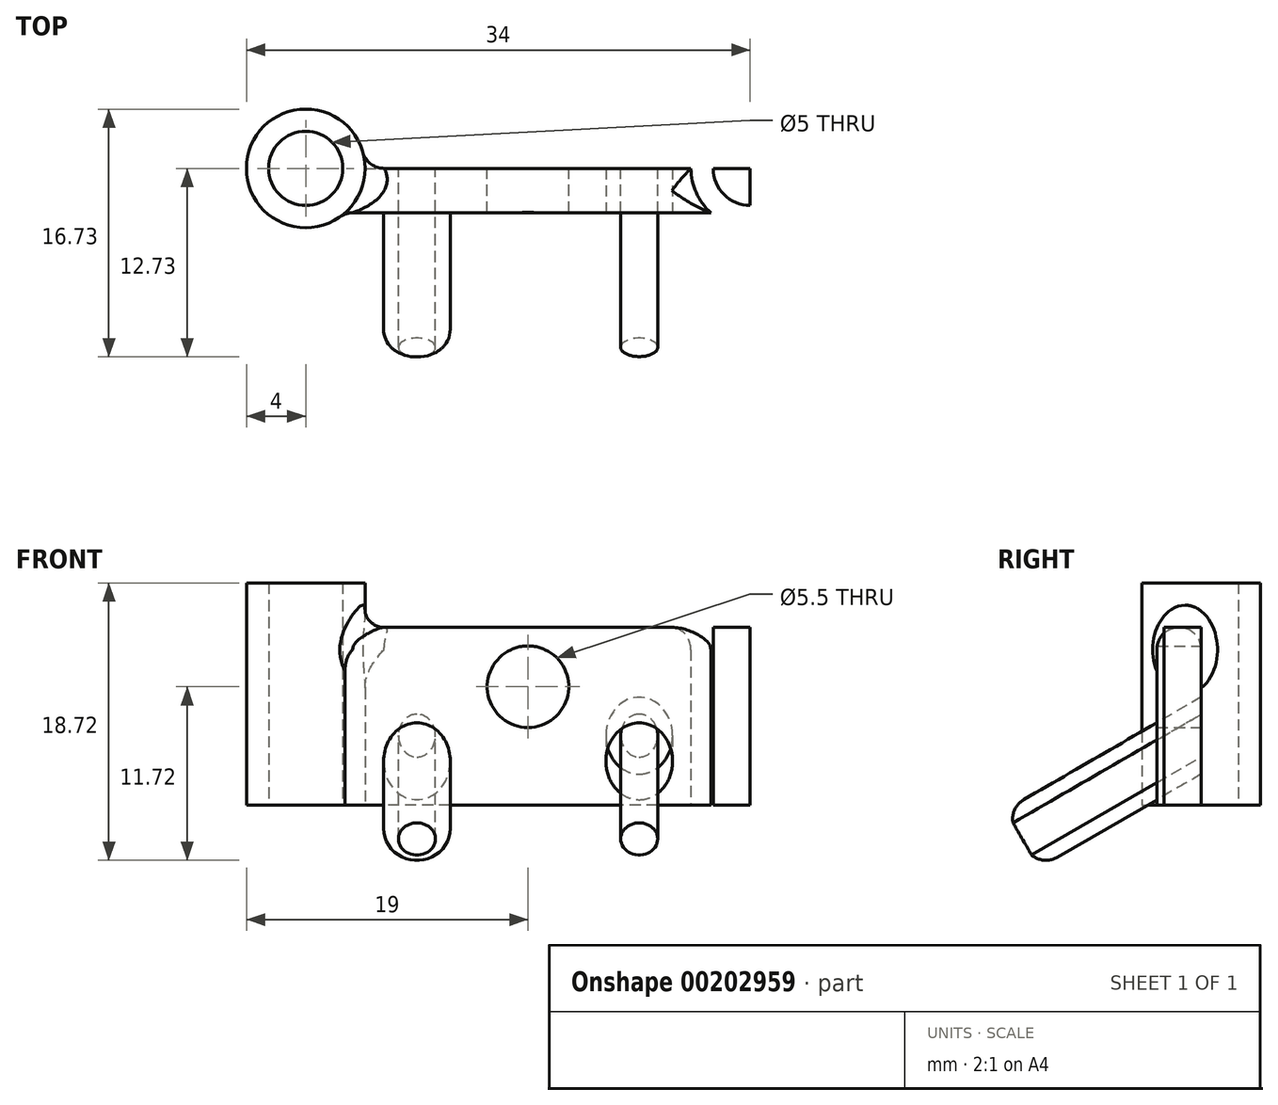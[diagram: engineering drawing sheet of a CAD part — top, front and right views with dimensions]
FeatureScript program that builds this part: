
annotation { "Feature Type Name" : "Feature", "Feature Type Description" : "" }
export const myFeature = defineFeature(function(context is Context, id is Id, definition is map)
    precondition{}
    {
        {
            var Q0;
            Q0=qCreatedBy(makeId("Top.planeOp"),FACE);
            var sketch = newSketch(context, id + "F0", { "sketchPlane" : qUnion([Q0])});
            skCircle(sketch, "E0", {"center": v(-15, 0) * mm, "radius": 2.5 * mm});
            skCircle(sketch, "E1", {"center": v(-15, 0) * mm, "radius": 4 * mm});
            skCircle(sketch, "E2.MirrorC", {"center": v(15, 0) * mm, "radius": 2.5 * mm});
            skCircle(sketch, "E3.MirrorC", {"center": v(15, 0) * mm, "radius": 4 * mm});
            skSolve(sketch);
        }
        {
            var Q0;
            Q0 = qSketchRegion(id + "F0", true);
            extrude(context, id + "F1", {"entities" : qUnion([Q0]), "depth" : 15 * mm, "offsetDistance" : 25 * mm});
        }
        {
            var Q0;
            Q0=qCreatedBy(makeId("Front.planeOp"),FACE);
            var sketch = newSketch(context, id + "F2", { "sketchPlane" : qUnion([Q0])});
            skLineSegment(sketch, "E4.bottom", {"start": v(15, 12) * mm, "end": v(-15, 12) * mm});
            skLineSegment(sketch, "E4.top", {"start": v(15, 0) * mm, "end": v(-15, 0) * mm});
            skLineSegment(sketch, "E4.left", {"start": v(15, 12) * mm, "end": v(15, 0) * mm});
            skLineSegment(sketch, "E4.right", {"start": v(-15, 12) * mm, "end": v(-15, 0) * mm});
            skPoint(sketch, "E4.middle", {"position": v(0, 6) * mm});
            skCircle(sketch, "E5", {"center": v(7.5, 6) * mm, "radius": 1.25 * mm});
            skCircle(sketch, "E6", {"center": v(7.5, 6) * mm, "radius": 2.25 * mm});
            skCircle(sketch, "E7.MirrorC", {"center": v(-7.5, 6) * mm, "radius": 1.25 * mm});
            skCircle(sketch, "E8.MirrorC", {"center": v(-7.5, 6) * mm, "radius": 2.25 * mm});
            skCircle(sketch, "E9", {"center": v(0, 8) * mm, "radius": 2.75 * mm});
            skSolve(sketch);
        }
        {
            var Q0;
            Q0=makeQuery(id+"F2.imprint","IMPRINT",FACE,{"disambiguationData":[TD([[makeQuery(id+"F2.imprint","IMPRINT",EDGE,{"derivedFrom":sQuery(id+"F2.wireOp",EDGE,"E4.bottom")}),1.0]])]});
            var Q1;
            Q1=makeQuery(id+"F2.imprint","IMPRINT",FACE,{"disambiguationData":[TD([[makeQuery(id+"F2.imprint","IMPRINT",EDGE,{"derivedFrom":sQuery(id+"F2.wireOp",EDGE,"E5")}),-1.0]])]});
            var Q2;
            Q2=makeQuery(id+"F2.imprint","IMPRINT",FACE,{"disambiguationData":[TD([[makeQuery(id+"F2.imprint","IMPRINT",EDGE,{"derivedFrom":sQuery(id+"F2.wireOp",EDGE,"E5")}),1.0]])]});
            var Q3;
            Q3=makeQuery(id+"F2.imprint","IMPRINT",FACE,{"disambiguationData":[TD([[makeQuery(id+"F2.imprint","IMPRINT",EDGE,{"derivedFrom":sQuery(id+"F2.wireOp",EDGE,"E7.MirrorC")}),1.0]])]});
            var Q4;
            Q4=makeQuery(id+"F2.imprint","IMPRINT",FACE,{"disambiguationData":[TD([[makeQuery(id+"F2.imprint","IMPRINT",EDGE,{"derivedFrom":sQuery(id+"F2.wireOp",EDGE,"E7.MirrorC")}),-1.0]])]});
            extrude(context, id + "F3", {"entities" : qUnion([Q0, Q1, Q2, Q3, Q4]), "depth" : 3 * mm, "offsetDistance" : 25 * mm});
        }
        {
            var Q0;
            Q0=qCreatedBy(makeId("Front.planeOp"),FACE);
            var Q1;
            Q1=makeQuery(id+"F3.opExtrude","CAP_EDGE",EDGE,{"disambiguationData":[OSD([sQuery(id+"F2.wireOp",EDGE,"E4.bottom")])],"isStart":false});
            cPlane(context, id + "F4", {"entities" : qUnion([Q0, Q1]), "cplaneType" : CPlaneType.LINE_ANGLE, "offset" : 25 * mm, "angle" : 30 * degree, "oppositeDirection" : true, "width" : 150 * mm, "height" : 150 * mm});
        }
        {
            var Q0;
            Q0=qCreatedBy(id+"F4.planeOp",FACE);
            var sketch = newSketch(context, id + "F5", { "sketchPlane" : qUnion([Q0])});
            skLineSegment(sketch, "E10.bottom", {"start": v(15, 13.07) * mm, "end": v(-15, 13.07) * mm});
            skLineSegment(sketch, "E10.top", {"start": v(15, 1.07) * mm, "end": v(-15, 1.07) * mm});
            skLineSegment(sketch, "E10.left", {"start": v(15, 13.07) * mm, "end": v(15, 1.07) * mm});
            skLineSegment(sketch, "E10.right", {"start": v(-15, 13.07) * mm, "end": v(-15, 1.07) * mm});
            skCircle(sketch, "E11", {"center": v(7.5, 4.07) * mm, "radius": 1.25 * mm});
            skCircle(sketch, "E12", {"center": v(7.5, 4.07) * mm, "radius": 2.25 * mm});
            skCircle(sketch, "E13.MirrorC", {"center": v(-7.5, 4.07) * mm, "radius": 1.25 * mm});
            skCircle(sketch, "E14.MirrorC", {"center": v(-7.5, 4.07) * mm, "radius": 2.25 * mm});
            skSolve(sketch);
        }
        {
            var Q0;
            Q0=makeQuery(id+"F5.imprint","IMPRINT",FACE,{"disambiguationData":[TD([[makeQuery(id+"F5.imprint","IMPRINT",EDGE,{"derivedFrom":sQuery(id+"F5.wireOp",EDGE,"E11")}),-1.0]])]});
            var Q1;
            Q1=makeQuery(id+"F5.imprint","IMPRINT",FACE,{"disambiguationData":[TD([[makeQuery(id+"F5.imprint","IMPRINT",EDGE,{"derivedFrom":sQuery(id+"F5.wireOp",EDGE,"E13.MirrorC")}),1.0]])]});
            extrude(context, id + "F6", {"entities" : qUnion([Q0, Q1]), "operationType" : NewBodyOperationType.ADD, "oppositeDirection" : true, "depth" : 15 * mm, "offsetDistance" : 25 * mm, "hasSecondDirection" : true, "secondDirectionOppositeDirection" : false, "secondDirectionDepth" : -3 * mm});
        }
        {
            var Q0;
            Q0=makeQuery(id+"F5.imprint","IMPRINT",FACE,{"disambiguationData":[TD([[makeQuery(id+"F5.imprint","IMPRINT",EDGE,{"derivedFrom":sQuery(id+"F5.wireOp",EDGE,"E11")}),1.0]])]});
            var Q1;
            Q1=makeQuery(id+"F5.imprint","IMPRINT",FACE,{"disambiguationData":[TD([[makeQuery(id+"F5.imprint","IMPRINT",EDGE,{"derivedFrom":sQuery(id+"F5.wireOp",EDGE,"E13.MirrorC")}),-1.0]])]});
            extrude(context, id + "F7", {"entities" : qUnion([Q0, Q1]), "operationType" : NewBodyOperationType.REMOVE, "depth" : 25 * mm, "offsetDistance" : 25 * mm, "hasSecondDirection" : true, "secondDirectionOppositeDirection" : true, "secondDirectionDepth" : 25 * mm});
        }
        {
            var Q0;
            Q0=makeQuery(id+"F3.opExtrude","SWEPT_BODY",BODY,{"disambiguationData":[OSD([sQuery(id+"F2.wireOp",EDGE,"E4.bottom"),sQuery(id+"F2.wireOp",EDGE,"E4.top"),sQuery(id+"F2.wireOp",EDGE,"E4.left"),sQuery(id+"F2.wireOp",EDGE,"E4.right"),sQuery(id+"F2.wireOp",EDGE,"6Aa2d1Ur-5F7A-H518-rewh-tOE36fWMP5cr")])]});
            var Q1;
            Q1=makeQuery(id+"F1.opExtrude","SWEPT_BODY",BODY,{"disambiguationData":[OSD([sQuery(id+"F0.wireOp",EDGE,"E2.MirrorC"),sQuery(id+"F0.wireOp",EDGE,"E3.MirrorC")])]});
            var Q2;
            Q2=makeQuery(id+"F1.opExtrude","SWEPT_BODY",BODY,{"disambiguationData":[OSD([sQuery(id+"F0.wireOp",EDGE,"E0"),sQuery(id+"F0.wireOp",EDGE,"E1")])]});
            booleanBodies(context, id + "F8", {"operationType" : BooleanOperationType.UNION, "tools" : qUnion([Q0, Q1, Q2])});
        }
        {
            var Q0;
            Q0=makeQuery(id+"F0.imprint","IMPRINT",FACE,{"disambiguationData":[TD([[makeQuery(id+"F0.imprint","IMPRINT",EDGE,{"derivedFrom":sQuery(id+"F0.wireOp",EDGE,"E0")}),1.0]])]});
            var Q1;
            Q1=makeQuery(id+"F0.imprint","IMPRINT",FACE,{"disambiguationData":[TD([[makeQuery(id+"F0.imprint","IMPRINT",EDGE,{"derivedFrom":sQuery(id+"F0.wireOp",EDGE,"E2.MirrorC")}),-1.0]])]});
            extrude(context, id + "F9", {"entities" : qUnion([Q0, Q1]), "operationType" : NewBodyOperationType.REMOVE, "oppositeDirection" : true, "depth" : 25 * mm, "offsetDistance" : 25 * mm, "hasSecondDirection" : true, "secondDirectionOppositeDirection" : false, "secondDirectionDepth" : 25 * mm});
        }
        {
            var Q0;
            {var subQ4=sQuery(id+"F2.wireOp",EDGE,"E4.bottom");Q0=makeQuery(id+"F8.opBoolean","SPLIT",FACE,{"disambiguationData":[TD([makeQuery(id+"F1.opExtrude","SWEPT_FACE",FACE,{"disambiguationData":[OSD([sQuery(id+"F0.wireOp",EDGE,"E1")])]})])],"derivedFrom":makeQuery(id+"F3.opExtrude","SWEPT_FACE",FACE,{"disambiguationData":[OSD([subQ4])]})});}
            var Q1;
            Q1=makeQuery(id+"F6.opExtrude","CAP_EDGE",EDGE,{"disambiguationData":[OSD([sQuery(id+"F5.wireOp",EDGE,"E12")])],"isStart":false});
            var Q2;
            Q2=makeQuery(id+"F6.opExtrude","CAP_EDGE",EDGE,{"disambiguationData":[OSD([sQuery(id+"F5.wireOp",EDGE,"E14.MirrorC")])],"isStart":false});
            fillet(context, id + "F10", {"entities" : qUnion([Q0, Q1, Q2]), "radius" : 1.5 * mm, "tangentPropagation" : true, "allowEdgeOverflow" : false});
        }
    });
